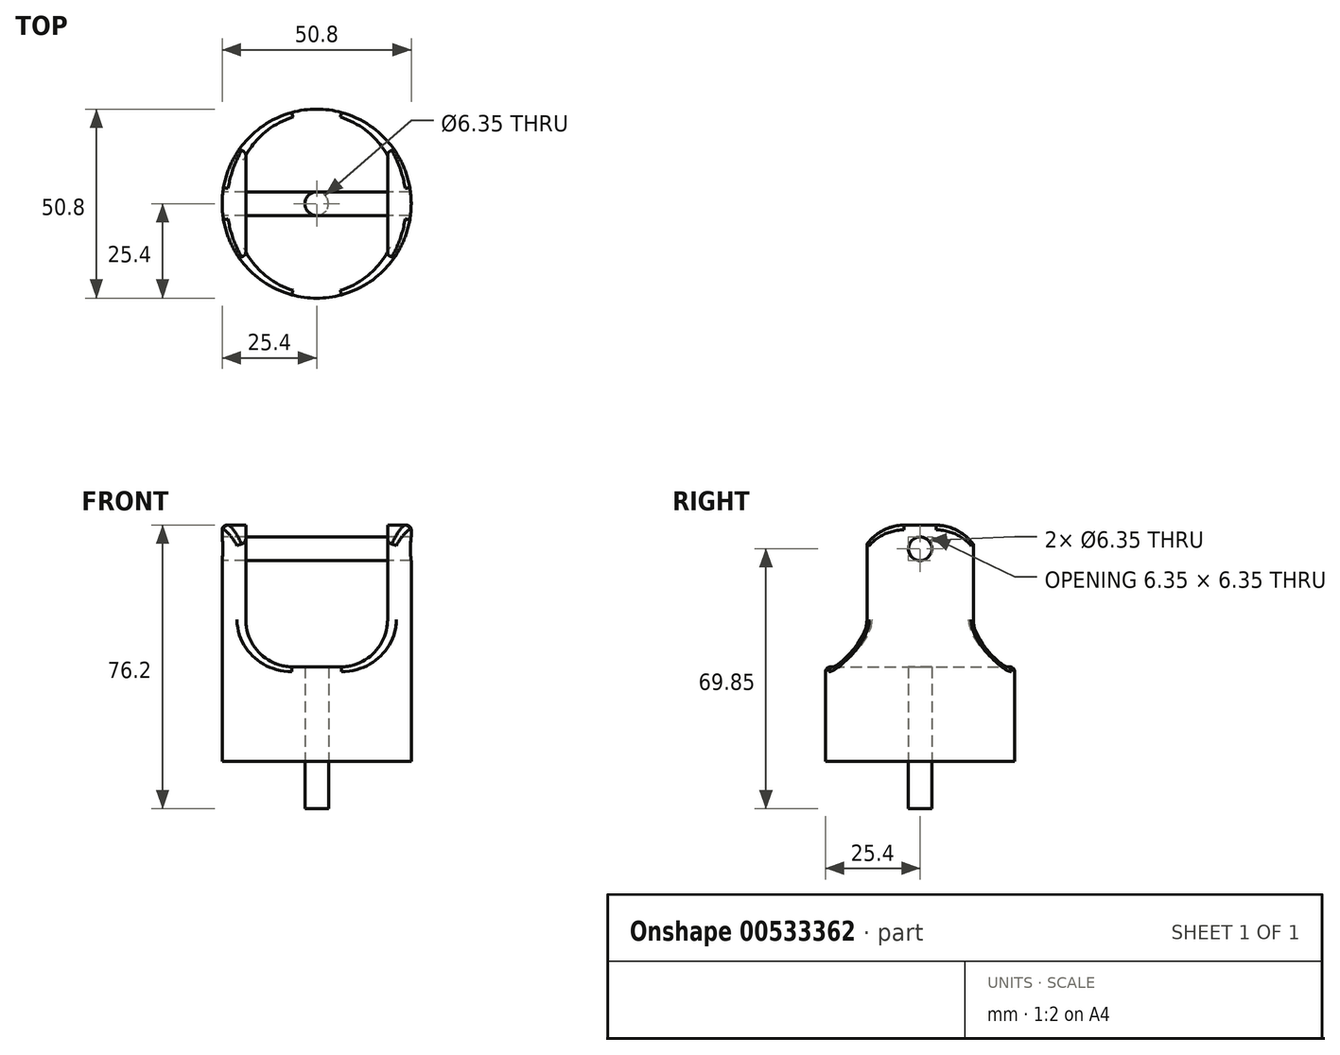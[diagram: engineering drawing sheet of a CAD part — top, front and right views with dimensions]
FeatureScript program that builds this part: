
annotation { "Feature Type Name" : "Feature", "Feature Type Description" : "" }
export const myFeature = defineFeature(function(context is Context, id is Id, definition is map)
    precondition{}
    {
        {
            var Q0;
            Q0=qCreatedBy(makeId("Top.planeOp"),FACE);
            var sketch = newSketch(context, id + "F0", { "sketchPlane" : qUnion([Q0])});
            skCircle(sketch, "E0", {"center": v(0, 0) * mm, "radius": 25.4 * mm});
            skLineSegment(sketch, "E1", {"start": v(19.05, 16.8) * mm, "end": v(19.05, -16.8) * mm});
            skLineSegment(sketch, "E2", {"start": v(-19.05, 16.8) * mm, "end": v(-19.05, -16.8) * mm});
            skSolve(sketch);
        }
        {
            var Q0;
            Q0 = qSketchRegion(id + "F0", true);
            extrude(context, id + "F1", {"entities" : qUnion([Q0]), "depth" : 25.4 * mm, "offsetDistance" : 25.4 * mm});
        }
        {
            var Q0;
            {var subQ0=sQuery(id+"F0.wireOp",EDGE,"E2");Q0=makeQuery(id+"F0.imprint","IMPRINT",FACE,{"disambiguationData":[TD([[makeQuery(id+"F0.imprint","IMPRINT",EDGE,{"derivedFrom":subQ0}),-1.0]])]});}
            var Q1;
            {var subQ0=sQuery(id+"F0.wireOp",EDGE,"E1");Q1=makeQuery(id+"F0.imprint","IMPRINT",FACE,{"disambiguationData":[TD([[makeQuery(id+"F0.imprint","IMPRINT",EDGE,{"derivedFrom":subQ0}),1.0]])]});}
            extrude(context, id + "F2", {"entities" : qUnion([Q0, Q1]), "operationType" : NewBodyOperationType.ADD, "depth" : 63.5 * mm, "offsetDistance" : 25.4 * mm});
        }
        {
            var Q0;
            Q0=makeQuery(id+"F2.opExtrude","SWEPT_FACE",FACE,{"disambiguationData":[OSD([sQuery(id+"F0.wireOp",EDGE,"E1")])]});
            var sketch = newSketch(context, id + "F3", { "sketchPlane" : qUnion([Q0])});
            skCircle(sketch, "E3", {"center": v(0, 57.15) * mm, "radius": 3.18 * mm});
            skPoint(sketch, "E3.centerSnap0", {"position": v(0, 63.5) * mm});
            skSolve(sketch);
        }
        {
            var Q0;
            Q0 = qSketchRegion(id + "F3", true);
            extrude(context, id + "F4", {"entities" : qUnion([Q0]), "operationType" : NewBodyOperationType.REMOVE, "endBound" : BoundingType.SYMMETRIC, "oppositeDirection" : true, "depth" : 152.4 * mm, "offsetDistance" : 25.4 * mm});
        }
        {
            var Q0;
            Q0=makeQuery(id+"F2.opExtrude","SWEPT_FACE",FACE,{"disambiguationData":[OSD([sQuery(id+"F0.wireOp",EDGE,"E1")])]});
            var sketch = newSketch(context, id + "F5", { "sketchPlane" : qUnion([Q0])});
            skLineSegment(sketch, "E4", {"start": v(-4.1, 63.5) * mm, "end": v(-4.1, 50.8) * mm, "construction": true});
            skLineSegment(sketch, "E5", {"start": v(-4.1, 50.8) * mm, "end": v(-16.8, 50.8) * mm, "construction": true});
            skArc(sketch, "E6", {"start": v(-16.8, 50.8) * mm, "mid": v(-12.75, 60.1) * mm, "end": v(-3.18, 63.47) * mm});
            skLineSegment(sketch, "E7", {"start": v(-4.1, 63.5) * mm, "end": v(-16.8, 63.5) * mm});
            skLineSegment(sketch, "E8", {"start": v(-16.8, 63.5) * mm, "end": v(-16.8, 50.8) * mm});
            skArc(sketch, "E9.MirrorCS", {"start": v(16.8, 50.8) * mm, "mid": v(12.75, 60.1) * mm, "end": v(3.18, 63.47) * mm});
            skLineSegment(sketch, "E10.MirrorCS", {"start": v(4.1, 63.5) * mm, "end": v(16.8, 63.5) * mm});
            skLineSegment(sketch, "E11.MirrorCS", {"start": v(16.8, 63.5) * mm, "end": v(16.8, 50.8) * mm});
            skSolve(sketch);
        }
        {
            var Q0;
            Q0 = qSketchRegion(id + "F5", true);
            extrude(context, id + "F6", {"entities" : qUnion([Q0]), "operationType" : NewBodyOperationType.REMOVE, "endBound" : BoundingType.SYMMETRIC, "oppositeDirection" : true, "depth" : 127 * mm, "offsetDistance" : 25.4 * mm});
        }
        {
            var Q0;
            Q0=makeQuery(id+"F1.opExtrude","CAP_FACE",FACE,{"disambiguationData":[OSD([sQuery(id+"F0.wireOp",EDGE,"E0")])],"isStart":true});
            var sketch = newSketch(context, id + "F7", { "sketchPlane" : qUnion([Q0])});
            skCircle(sketch, "E12", {"center": v(0, 0) * mm, "radius": 3.18 * mm});
            skSolve(sketch);
        }
        {
            var Q0;
            Q0 = qSketchRegion(id + "F7", true);
            extrude(context, id + "F8", {"entities" : qUnion([Q0]), "operationType" : NewBodyOperationType.REMOVE, "oppositeDirection" : true, "depth" : 25.4 * mm, "offsetDistance" : 25.4 * mm});
        }
        {
            var Q0;
            Q0=makeQuery(id+"F2.boolean.opBoolean","INTERSECT",EDGE,{"derivedFrom":[makeQuery(id+"F1.opExtrude","CAP_FACE",FACE,{"disambiguationData":[OSD([sQuery(id+"F0.wireOp",EDGE,"E0")])],"isStart":false}),makeQuery(id+"F2.opExtrude","SWEPT_FACE",FACE,{"disambiguationData":[OSD([sQuery(id+"F0.wireOp",EDGE,"E2")])]})]});
            var Q1;
            Q1=makeQuery(id+"F2.boolean.opBoolean","INTERSECT",EDGE,{"derivedFrom":[makeQuery(id+"F1.opExtrude","CAP_FACE",FACE,{"disambiguationData":[OSD([sQuery(id+"F0.wireOp",EDGE,"E0")])],"isStart":false}),makeQuery(id+"F2.opExtrude","SWEPT_FACE",FACE,{"disambiguationData":[OSD([sQuery(id+"F0.wireOp",EDGE,"E1")])]})]});
            fillet(context, id + "F9", {"entities" : qUnion([Q0, Q1]), "radius" : 12.7 * mm, "tangentPropagation" : true, "allowEdgeOverflow" : false});
        }
        {
            var Q0;
            {var subQ0=sQuery(id+"F0.wireOp",EDGE,"E2");var subQ1=sQuery(id+"F0.wireOp",EDGE,"E0");Q0=makeQuery(id+"F2.opExtrude","SWEPT_EDGE",EDGE,{"disambiguationData":[OSD([subQ1,subQ0]),TDD([makeQuery(id+"F0.imprint","INTERSECT",VERTEX,{"disambiguationData":[OD(0.0)],"derivedFrom":[subQ1,subQ0]})])]});}
            var Q1;
            {var subQ0=sQuery(id+"F0.wireOp",EDGE,"E2");var subQ1=sQuery(id+"F0.wireOp",EDGE,"E0");Q1=makeQuery(id+"F2.opExtrude","SWEPT_EDGE",EDGE,{"disambiguationData":[OSD([subQ1,subQ0]),TDD([makeQuery(id+"F0.imprint","INTERSECT",VERTEX,{"disambiguationData":[OD(1.0)],"derivedFrom":[subQ1,subQ0]})])]});}
            var Q2;
            {var subQ0=sQuery(id+"F0.wireOp",EDGE,"E1");var subQ1=sQuery(id+"F0.wireOp",EDGE,"E0");Q2=makeQuery(id+"F2.opExtrude","CAP_EDGE",EDGE,{"disambiguationData":[OSD([subQ1]),TDD([makeQuery(id+"F0.imprint","IMPRINT",EDGE,{"disambiguationData":[TD([[makeQuery(id+"F0.imprint","INTERSECT",VERTEX,{"disambiguationData":[OD(0.0)],"derivedFrom":[subQ1,subQ0]}),1.0]])],"derivedFrom":subQ1})])],"isStart":false});}
            var Q3;
            {var subQ0=sQuery(id+"F0.wireOp",EDGE,"E2");var subQ1=sQuery(id+"F0.wireOp",EDGE,"E0");Q3=makeQuery(id+"F2.opExtrude","CAP_EDGE",EDGE,{"disambiguationData":[OSD([subQ1]),TDD([makeQuery(id+"F0.imprint","IMPRINT",EDGE,{"disambiguationData":[TD([[makeQuery(id+"F0.imprint","INTERSECT",VERTEX,{"disambiguationData":[OD(0.0)],"derivedFrom":[subQ1,subQ0]}),-1.0]])],"derivedFrom":subQ1})])],"isStart":false});}
            fillet(context, id + "F10", {"entities" : qUnion([Q0, Q1, Q2, Q3]), "radius" : 1.27 * mm, "tangentPropagation" : true, "allowEdgeOverflow" : false});
        }
        {
            var Q0;
            Q0=makeQuery(id+"F2.opExtrude","SWEPT_FACE",FACE,{"disambiguationData":[OSD([sQuery(id+"F0.wireOp",EDGE,"E1")])]});
            var sketch = newSketch(context, id + "F11", { "sketchPlane" : qUnion([Q0])});
            skCircle(sketch, "E13", {"center": v(0, 57.15) * mm, "radius": 3.18 * mm});
            skSolve(sketch);
        }
        {
            var Q0;
            Q0 = qSketchRegion(id + "F11", true);
            extrude(context, id + "F12", {"entities" : qUnion([Q0]), "depth" : 38.1 * mm, "offsetDistance" : 25.4 * mm});
        }
        {
            var Q0;
            Q0=makeQuery(id+"F1.opExtrude","CAP_FACE",FACE,{"disambiguationData":[OSD([sQuery(id+"F0.wireOp",EDGE,"E0")])],"isStart":true});
            var sketch = newSketch(context, id + "F13", { "sketchPlane" : qUnion([Q0])});
            skCircle(sketch, "E14", {"center": v(0, 0) * mm, "radius": 3.18 * mm});
            skSolve(sketch);
        }
        {
            var Q0;
            Q0 = qSketchRegion(id + "F13", true);
            extrude(context, id + "F14", {"entities" : qUnion([Q0]), "depth" : 12.7 * mm, "offsetDistance" : 25.4 * mm});
        }
    });
